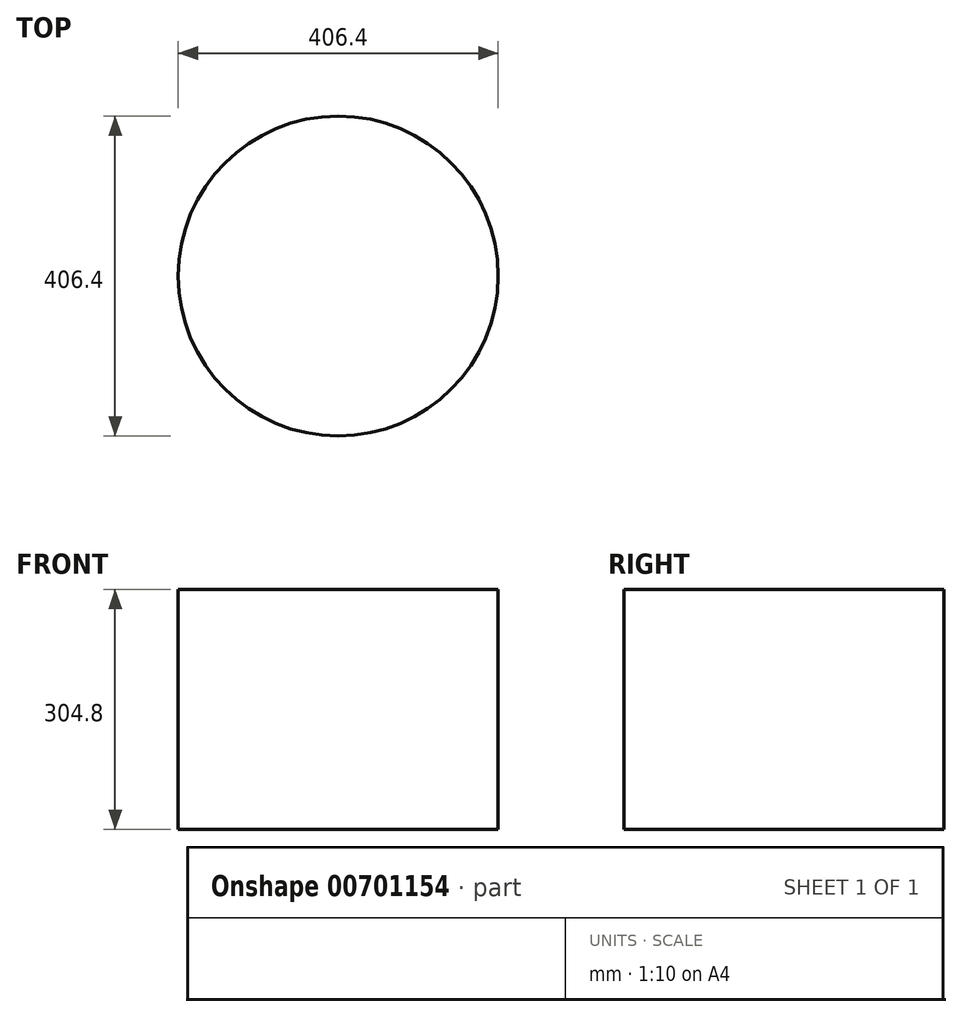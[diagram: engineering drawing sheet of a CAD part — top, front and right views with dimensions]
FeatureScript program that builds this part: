
annotation { "Feature Type Name" : "Feature", "Feature Type Description" : "" }
export const myFeature = defineFeature(function(context is Context, id is Id, definition is map)
    precondition{}
    {
        {
            var Q0;
            Q0=qCreatedBy(makeId("Top.planeOp"),FACE);
            var sketch = newSketch(context, id + "F0", { "sketchPlane" : qUnion([Q0])});
            skCircle(sketch, "E0", {"center": v(0, 0) * mm, "radius": 203.2 * mm});
            skSolve(sketch);
        }
        {
            var Q0;
            Q0 = qSketchRegion(id + "F0", true);
            extrude(context, id + "F1", {"entities" : qUnion([Q0]), "depth" : 304.8 * mm, "offsetDistance" : 25.4 * mm});
        }
    });
